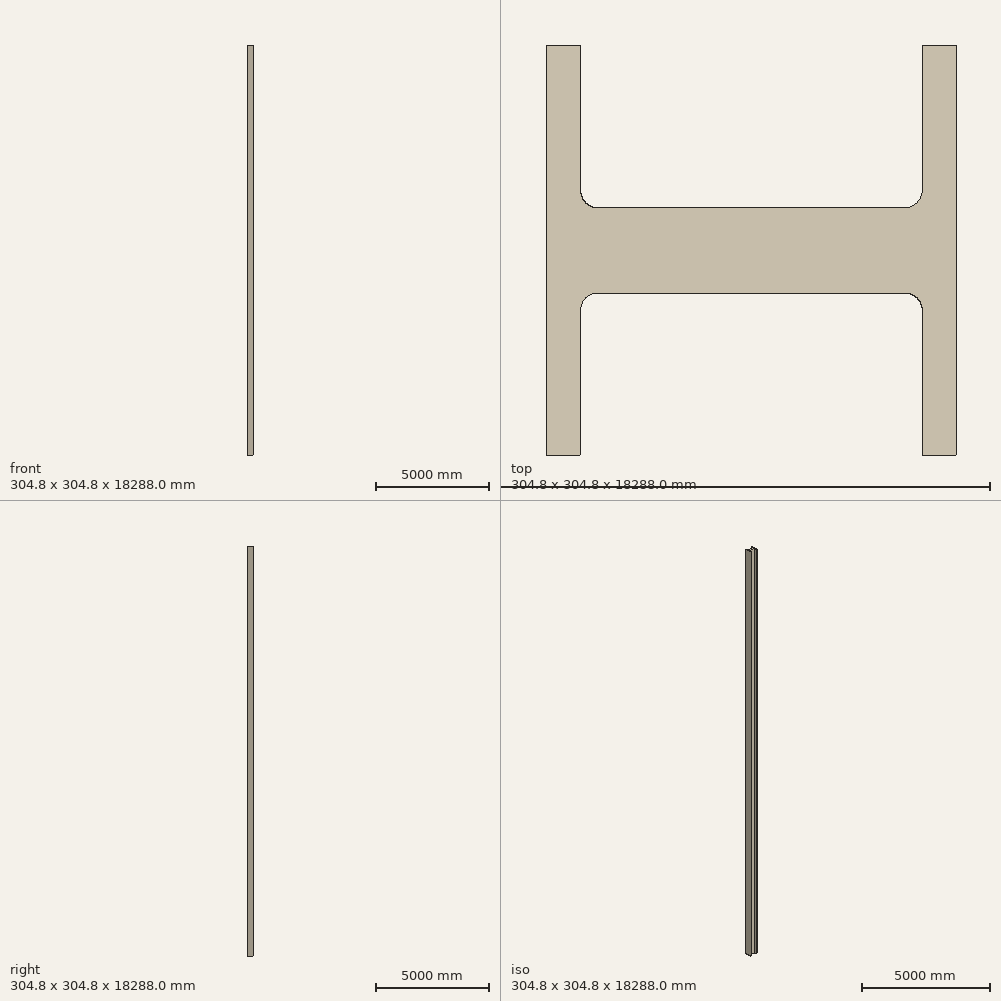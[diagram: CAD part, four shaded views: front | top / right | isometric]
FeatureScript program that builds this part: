
annotation { "Feature Type Name" : "Feature", "Feature Type Description" : "" }
export const myFeature = defineFeature(function(context is Context, id is Id, definition is map)
    precondition{}
    {
        {
            var Q0;
            Q0=qCreatedBy(makeId("Top.planeOp"),FACE);
            var sketch = newSketch(context, id + "F0", { "sketchPlane" : qUnion([Q0])});
            skLineSegment(sketch, "E0.bottom", {"start": v(152.4, 152.4) * mm, "end": v(-152.4, 152.4) * mm});
            skLineSegment(sketch, "E0.top", {"start": v(152.4, -152.4) * mm, "end": v(-152.4, -152.4) * mm});
            skLineSegment(sketch, "E0.left", {"start": v(152.4, 152.4) * mm, "end": v(152.4, -152.4) * mm});
            skLineSegment(sketch, "E0.right", {"start": v(-152.4, 152.4) * mm, "end": v(-152.4, -152.4) * mm});
            skPoint(sketch, "E0.middle", {"position": v(0, 0) * mm});
            skLineSegment(sketch, "E1", {"start": v(-127, 152.4) * mm, "end": v(-127, -152.4) * mm});
            skLineSegment(sketch, "E2", {"start": v(127, 152.4) * mm, "end": v(127, -152.4) * mm});
            skLineSegment(sketch, "E3.bottom", {"start": v(127, 31.75) * mm, "end": v(-127, 31.75) * mm});
            skLineSegment(sketch, "E3.top", {"start": v(127, -31.75) * mm, "end": v(-127, -31.75) * mm});
            skLineSegment(sketch, "E3.left", {"start": v(127, 31.75) * mm, "end": v(127, -31.75) * mm});
            skLineSegment(sketch, "E3.right", {"start": v(-127, 31.75) * mm, "end": v(-127, -31.75) * mm});
            skSolve(sketch);
        }
        {
            var Q0;
            {var subQ4=sQuery(id+"F0.wireOp",EDGE,"E0.right");Q0=makeQuery(id+"F0.imprint","IMPRINT",FACE,{"disambiguationData":[TD([[makeQuery(id+"F0.imprint","IMPRINT",EDGE,{"derivedFrom":subQ4}),1.0]])]});}
            var Q1;
            Q1=makeQuery(id+"F0.imprint","IMPRINT",FACE,{"disambiguationData":[TD([[makeQuery(id+"F0.imprint","IMPRINT",EDGE,{"derivedFrom":sQuery(id+"F0.wireOp",EDGE,"E3.bottom")}),1.0]])]});
            var Q2;
            {var subQ4=sQuery(id+"F0.wireOp",EDGE,"E0.left");Q2=makeQuery(id+"F0.imprint","IMPRINT",FACE,{"disambiguationData":[TD([[makeQuery(id+"F0.imprint","IMPRINT",EDGE,{"derivedFrom":subQ4}),-1.0]])]});}
            extrude(context, id + "F1", {"entities" : qUnion([Q0, Q1, Q2]), "depth" : 18288 * mm});
        }
        {
            var Q0;
            Q0=makeQuery(id+"F1.opExtrude","SWEPT_EDGE",EDGE,{"disambiguationData":[OSD([sQuery(id+"F0.wireOp",EDGE,"E1"),sQuery(id+"F0.wireOp",EDGE,"E3.top"),sQuery(id+"F0.wireOp",EDGE,"E3.right")])]});
            var Q1;
            Q1=makeQuery(id+"F1.opExtrude","SWEPT_EDGE",EDGE,{"disambiguationData":[OSD([sQuery(id+"F0.wireOp",EDGE,"E2"),sQuery(id+"F0.wireOp",EDGE,"E3.top"),sQuery(id+"F0.wireOp",EDGE,"E3.left")])]});
            var Q2;
            Q2=makeQuery(id+"F1.opExtrude","SWEPT_EDGE",EDGE,{"disambiguationData":[OSD([sQuery(id+"F0.wireOp",EDGE,"E1"),sQuery(id+"F0.wireOp",EDGE,"E3.bottom"),sQuery(id+"F0.wireOp",EDGE,"E3.right")])]});
            var Q3;
            Q3=makeQuery(id+"F1.opExtrude","SWEPT_EDGE",EDGE,{"disambiguationData":[OSD([sQuery(id+"F0.wireOp",EDGE,"E2"),sQuery(id+"F0.wireOp",EDGE,"E3.bottom"),sQuery(id+"F0.wireOp",EDGE,"E3.left")])]});
            fillet(context, id + "F2", {"entities" : qUnion([Q0, Q1, Q2, Q3]), "radius" : 12.7 * mm, "tangentPropagation" : true, "allowEdgeOverflow" : false});
        }
    });
